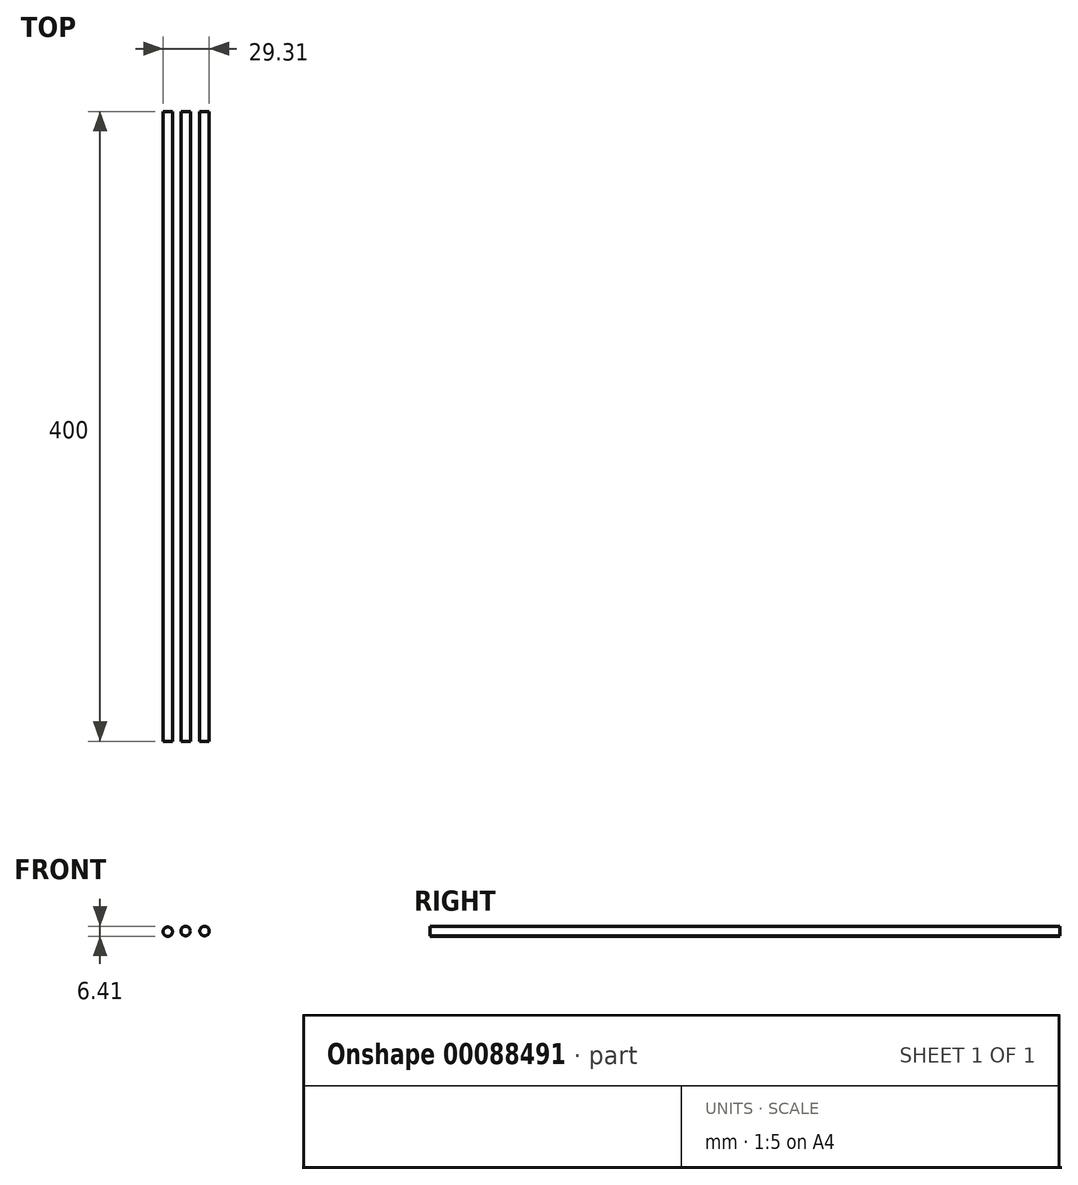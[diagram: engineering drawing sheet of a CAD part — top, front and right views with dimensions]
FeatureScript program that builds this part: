
annotation { "Feature Type Name" : "Feature", "Feature Type Description" : "" }
export const myFeature = defineFeature(function(context is Context, id is Id, definition is map)
    precondition{}
    {
        {
            var Q0;
            Q0=qCreatedBy(makeId("Front.planeOp"),FACE);
            var sketch = newSketch(context, id + "F0", { "sketchPlane" : qUnion([Q0])});
            skCircle(sketch, "E0", {"center": v(0, 0) * mm, "radius": 3 * mm});
            skSolve(sketch);
        }
        {
            var Q0;
            Q0=makeQuery(id+"F0.imprint","IMPRINT",FACE,{"disambiguationData":[TD([[makeQuery(id+"F0.imprint","IMPRINT",EDGE,{"derivedFrom":sQuery(id+"F0.wireOp",EDGE,"E0")}),1.0]])]});
            extrude(context, id + "F1", {"entities" : qUnion([Q0]), "endBound" : BoundingType.SYMMETRIC, "depth" : 400 * mm});
        }
        {
            var Q0;
            Q0=qCreatedBy(makeId("Front.planeOp"),FACE);
            var sketch = newSketch(context, id + "F2", { "sketchPlane" : qUnion([Q0])});
            skCircle(sketch, "E1", {"center": v(-12, 0) * mm, "radius": 3 * mm});
            skSolve(sketch);
        }
        {
            var Q0;
            Q0 = qSketchRegion(id + "F2", true);
            extrude(context, id + "F3", {"entities" : qUnion([Q0]), "endBound" : BoundingType.SYMMETRIC, "depth" : 400 * mm});
        }
        {
            var Q0;
            Q0=qCreatedBy(makeId("Front.planeOp"),FACE);
            var sketch = newSketch(context, id + "F4", { "sketchPlane" : qUnion([Q0])});
            skCircle(sketch, "E2", {"center": v(-23.31, -0.4) * mm, "radius": 3 * mm});
            skSolve(sketch);
        }
        {
            var Q0;
            Q0=makeQuery(id+"F4.imprint","IMPRINT",FACE,{"disambiguationData":[TD([[makeQuery(id+"F4.imprint","IMPRINT",EDGE,{"derivedFrom":sQuery(id+"F4.wireOp",EDGE,"E2")}),1.0]])]});
            extrude(context, id + "F5", {"entities" : qUnion([Q0]), "endBound" : BoundingType.SYMMETRIC, "depth" : 400 * mm});
        }
    });
